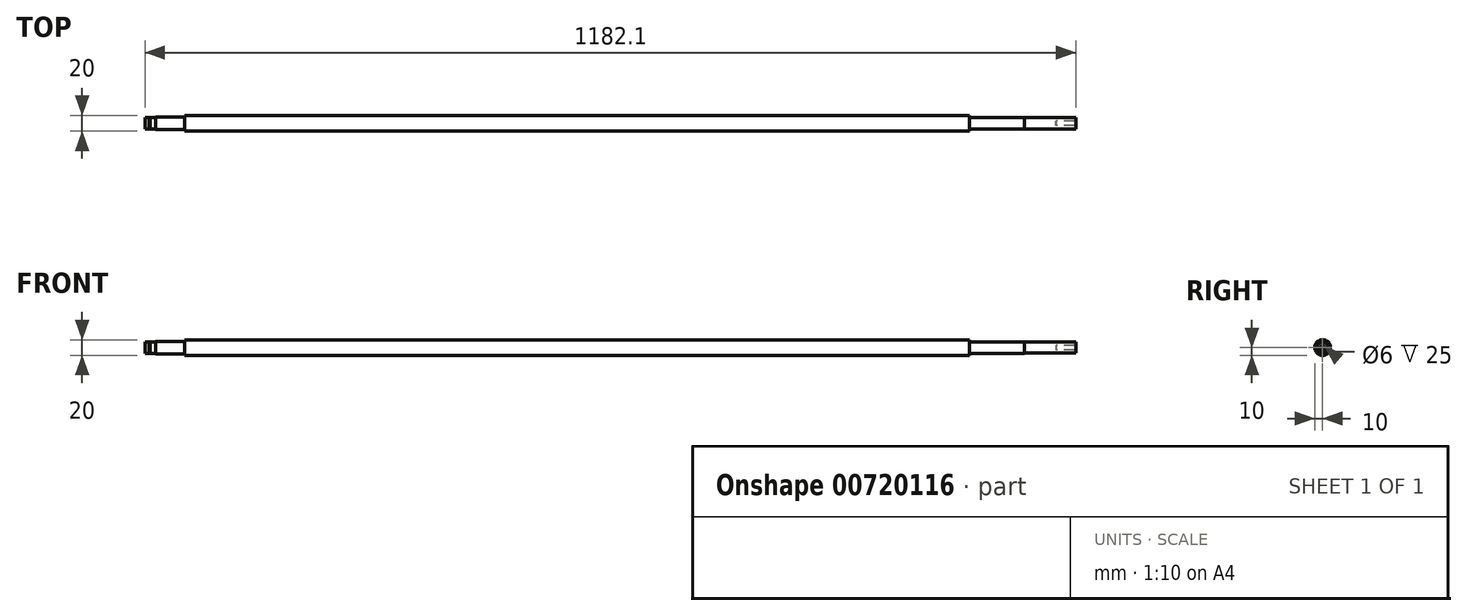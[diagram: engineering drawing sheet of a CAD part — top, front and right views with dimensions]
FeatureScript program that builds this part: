
annotation { "Feature Type Name" : "Feature", "Feature Type Description" : "" }
export const myFeature = defineFeature(function(context is Context, id is Id, definition is map)
    precondition{}
    {
        {
            var Q0;
            Q0=qCreatedBy(makeId("Front.planeOp"),FACE);
            var sketch = newSketch(context, id + "F0", { "sketchPlane" : qUnion([Q0])});
            skLineSegment(sketch, "E0", {"start": v(0, 0) * mm, "end": v(0, 7.5) * mm});
            skLineSegment(sketch, "E1", {"start": v(0, 7.5) * mm, "end": v(5, 7.5) * mm});
            skLineSegment(sketch, "E2", {"start": v(5, 7.5) * mm, "end": v(5, 7.15) * mm});
            skLineSegment(sketch, "E3", {"start": v(5, 7.15) * mm, "end": v(6.1, 7.15) * mm});
            skLineSegment(sketch, "E4", {"start": v(6.1, 7.15) * mm, "end": v(6.1, 7.5) * mm});
            skLineSegment(sketch, "E5", {"start": v(6.1, 7.5) * mm, "end": v(13.1, 7.5) * mm});
            skLineSegment(sketch, "E6", {"start": v(13.1, 7.5) * mm, "end": v(13.1, 8) * mm});
            skLineSegment(sketch, "E7", {"start": v(13.1, 8) * mm, "end": v(50.1, 8) * mm});
            skLineSegment(sketch, "E8", {"start": v(50.1, 8) * mm, "end": v(50.1, 10) * mm});
            skLineSegment(sketch, "E9", {"start": v(50.1, 10) * mm, "end": v(1047.1, 10) * mm});
            skLineSegment(sketch, "E10", {"start": v(1047.1, 10) * mm, "end": v(1047.1, 7.5) * mm});
            skLineSegment(sketch, "E11", {"start": v(1047.1, 7.5) * mm, "end": v(1117.1, 7.5) * mm});
            skLineSegment(sketch, "E12", {"start": v(0, 0) * mm, "end": v(1157.1, 0) * mm});
            skLineSegment(sketch, "E13", {"start": v(1117.1, 7.5) * mm, "end": v(1117.1, 7) * mm});
            skLineSegment(sketch, "E14", {"start": v(1117.1, 7) * mm, "end": v(1182.1, 7) * mm});
            skLineSegment(sketch, "E15", {"start": v(1182.1, 7) * mm, "end": v(1182.1, 3) * mm});
            skLineSegment(sketch, "E16", {"start": v(1157.1, 0) * mm, "end": v(1157.1, 3) * mm});
            skLineSegment(sketch, "E17", {"start": v(1157.1, 3) * mm, "end": v(1182.1, 3) * mm});
            skPoint(sketch, "E18.orphan", {"position": v(1182.1, 0) * mm});
            skSolve(sketch);
        }
        {
            var Q0;
            Q0 = qSketchRegion(id + "F0", true);
            var Q1;
            Q1=sQuery(id+"F0.wireOp",EDGE,"E12");
            revolve(context, id + "F1", {"surfaceOperationType" : NewSurfaceOperationType.NEW, "entities" : qUnion([Q0]), "axis" : qUnion([Q1]), "revolveType" : RevolveType.FULL});
        }
    });
